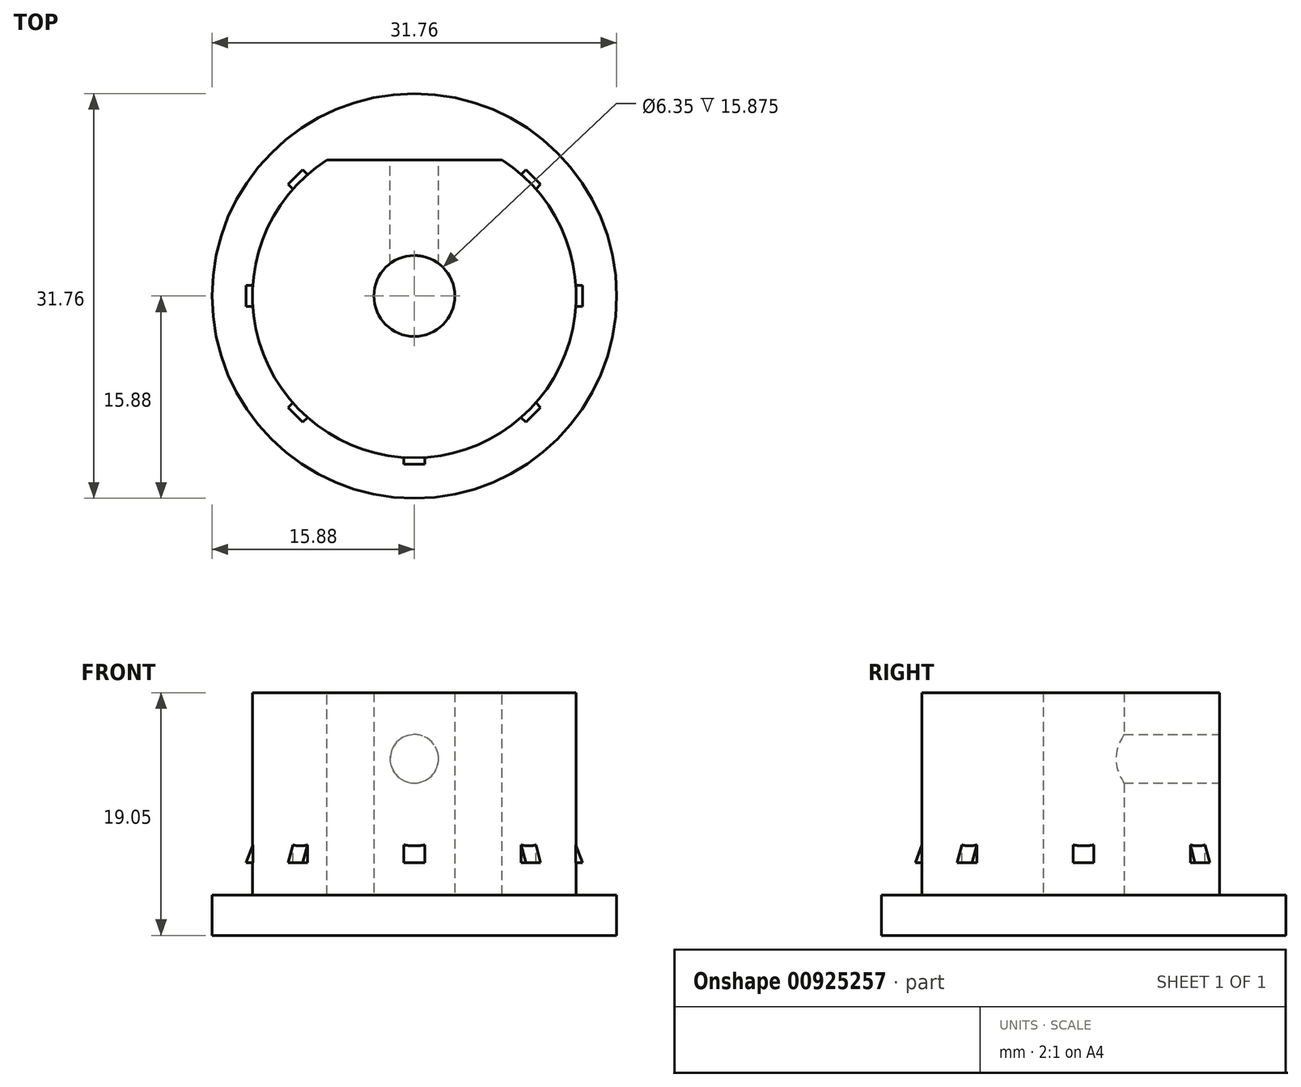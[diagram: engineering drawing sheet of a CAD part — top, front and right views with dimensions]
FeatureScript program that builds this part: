
annotation { "Feature Type Name" : "Feature", "Feature Type Description" : "" }
export const myFeature = defineFeature(function(context is Context, id is Id, definition is map)
    precondition{}
    {
        {
            var Q0;
            Q0=qCreatedBy(makeId("Top.planeOp"),FACE);
            var sketch = newSketch(context, id + "F0", { "sketchPlane" : qUnion([Q0])});
            skCircle(sketch, "E0", {"center": v(0, 0) * mm, "radius": 15.88 * mm});
            skCircle(sketch, "E1", {"center": v(0, 0) * mm, "radius": 12.7 * mm});
            skCircle(sketch, "E2", {"center": v(0, 0) * mm, "radius": 3.18 * mm});
            skSolve(sketch);
        }
        {
            var Q0;
            Q0=makeQuery(id+"F0.imprint","IMPRINT",FACE,{"disambiguationData":[TD([[makeQuery(id+"F0.imprint","IMPRINT",EDGE,{"derivedFrom":sQuery(id+"F0.wireOp",EDGE,"E1")}),1.0]])]});
            extrude(context, id + "F1", {"entities" : qUnion([Q0]), "depth" : 19.05 * mm, "offsetDistance" : 25.4 * mm});
        }
        {
            var Q0;
            Q0=makeQuery(id+"F0.imprint","IMPRINT",FACE,{"disambiguationData":[TD([[makeQuery(id+"F0.imprint","IMPRINT",EDGE,{"derivedFrom":sQuery(id+"F0.wireOp",EDGE,"E0")}),1.0]])]});
            extrude(context, id + "F2", {"entities" : qUnion([Q0]), "operationType" : NewBodyOperationType.ADD, "depth" : 3.17 * mm, "offsetDistance" : 25.4 * mm});
        }
        {
            var Q0;
            Q0=makeQuery(id+"F1.opExtrude","CAP_FACE",FACE,{"disambiguationData":[OSD([sQuery(id+"F0.wireOp",EDGE,"E1")])],"isStart":false});
            var sketch = newSketch(context, id + "F3", { "sketchPlane" : qUnion([Q0])});
            skLineSegment(sketch, "E3", {"start": v(-6.87, 10.68) * mm, "end": v(6.87, 10.68) * mm});
            skSolve(sketch);
        }
        {
            var Q0;
            {var subQ0=sQuery(id+"F3.wireOp",EDGE,"E3");Q0=makeQuery(id+"F3.imprint","IMPRINT",FACE,{"disambiguationData":[TD([[makeQuery(id+"F3.imprint","IMPRINT",EDGE,{"derivedFrom":subQ0}),1.0]])]});}
            extrude(context, id + "F4", {"entities" : qUnion([Q0]), "operationType" : NewBodyOperationType.REMOVE, "oppositeDirection" : true, "depth" : 12.7 * mm, "offsetDistance" : 25.4 * mm});
        }
        {
            var Q0;
            Q0=makeQuery(id+"F0.imprint","IMPRINT",FACE,{"disambiguationData":[TD([[makeQuery(id+"F0.imprint","IMPRINT",EDGE,{"derivedFrom":sQuery(id+"F0.wireOp",EDGE,"E2")}),1.0]])]});
            extrude(context, id + "F5", {"entities" : qUnion([Q0]), "operationType" : NewBodyOperationType.ADD, "depth" : 3.17 * mm, "offsetDistance" : 25.4 * mm});
        }
        {
            var Q0;
            Q0=makeQuery(id+"F4.boolean.opBoolean","COPY",FACE,{"derivedFrom":makeQuery(id+"F4.opExtrude","SWEPT_FACE",FACE,{"disambiguationData":[OSD([sQuery(id+"F3.wireOp",EDGE,"E3")])]})});
            var sketch = newSketch(context, id + "F6", { "sketchPlane" : qUnion([Q0])});
            skCircle(sketch, "E4", {"center": v(0, 13.86) * mm, "radius": 1.9 * mm});
            skSolve(sketch);
        }
        {
            var Q0;
            Q0=makeQuery(id+"F6.imprint","IMPRINT",FACE,{"disambiguationData":[TD([[makeQuery(id+"F6.imprint","IMPRINT",EDGE,{"derivedFrom":sQuery(id+"F6.wireOp",EDGE,"E4")}),1.0]])]});
            extrude(context, id + "F7", {"entities" : qUnion([Q0]), "operationType" : NewBodyOperationType.REMOVE, "oppositeDirection" : true, "depth" : 12.7 * mm, "offsetDistance" : 25.4 * mm});
        }
        {
            var Q0;
            Q0=makeQuery(id+"F1.opExtrude","CAP_FACE",FACE,{"disambiguationData":[OSD([sQuery(id+"F0.wireOp",EDGE,"E1"),sQuery(id+"F0.wireOp",EDGE,"E2")])],"isStart":false});
            var sketch = newSketch(context, id + "F8", { "sketchPlane" : qUnion([Q0])});
            skLineSegment(sketch, "E5", {"start": v(-12.7, 0) * mm, "end": v(12.7, 0) * mm, "construction": true});
            skLineSegment(sketch, "E6", {"start": v(12.7, 0) * mm, "end": v(13.2, 0) * mm, "construction": true});
            skLineSegment(sketch, "E7.left", {"start": v(13.2, 0.82) * mm, "end": v(13.2, -0.82) * mm});
            skPoint(sketch, "E7.middle", {"position": v(12.7, 0) * mm});
            skPoint(sketch, "E8.orphan", {"position": v(12.2, 0.82) * mm});
            skPoint(sketch, "E7.top.end.orphan", {"position": v(12.2, -0.82) * mm});
            skLineSegment(sketch, "E9", {"start": v(13.2, -0.82) * mm, "end": v(12.67, -0.82) * mm});
            skLineSegment(sketch, "E10", {"start": v(13.2, 0.82) * mm, "end": v(12.67, 0.82) * mm});
            skSolve(sketch);
        }
        {
            var Q0;
            Q0=makeQuery(id+"F8.imprint","IMPRINT",FACE,{"disambiguationData":[TD([[makeQuery(id+"F8.imprint","IMPRINT",EDGE,{"derivedFrom":sQuery(id+"F8.wireOp",EDGE,"E7.left")}),-1.0]])]});
            extrude(context, id + "F9", {"entities" : qUnion([Q0]), "oppositeDirection" : true, "depth" : 13.33 * mm, "offsetDistance" : 25.4 * mm});
        }
        {
            var Q0;
            Q0=makeQuery(id+"F9.opExtrude","CAP_EDGE",EDGE,{"disambiguationData":[OSD([sQuery(id+"F8.wireOp",EDGE,"E7.left")])],"isStart":true});
            chamfer(context, id + "F10", {"entities" : qUnion([Q0]), "chamferType" : ChamferType.TWO_OFFSETS, "width1" : 13.33 * mm, "oppositeDirection" : false, "width2" : 5.08 * mm, "tangentPropagation" : true});
        }
        {
            var Q0;
            Q0=qCreatedBy(makeId("Right.planeOp"),FACE);
            var sketch = newSketch(context, id + "F11", { "sketchPlane" : qUnion([Q0])});
            skLineSegment(sketch, "E11", {"start": v(0, 0) * mm, "end": v(0, 25.06) * mm, "construction": true});
            skSolve(sketch);
        }
        {
            var Q0;
            Q0=makeQuery(id+"F9.opExtrude","SWEPT_BODY",BODY,{"disambiguationData":[OSD([sQuery(id+"F0.wireOp",EDGE,"E1"),sQuery(id+"F8.wireOp",EDGE,"E7.left"),sQuery(id+"F8.wireOp",EDGE,"E9"),sQuery(id+"F8.wireOp",EDGE,"E10")])]});
            var Q1;
            Q1=sQuery(id+"F11.wireOp",EDGE,"E11");
            circularPattern(context, id + "F12", {"entities" : qUnion([Q0]), "axis" : qUnion([Q1]), "angle" : 360 * degree, "instanceCount" : 8, "equalSpace" : true, "computeTransformsWithoutBuiltin" : true});
        }
        {
            var Q0;
            Q0=makeQuery(id+"F12.opPattern","COPY",BODY,{"derivedFrom":makeQuery(id+"F9.opExtrude","SWEPT_BODY",BODY,{"disambiguationData":[OSD([sQuery(id+"F0.wireOp",EDGE,"E1"),sQuery(id+"F8.wireOp",EDGE,"E7.left"),sQuery(id+"F8.wireOp",EDGE,"E9"),sQuery(id+"F8.wireOp",EDGE,"E10")])]}),"instanceName":"2"});
            deleteBodies(context, id + "F13", {"entities" : qUnion([Q0])});
        }
        {
            var Q0;
            Q0=makeQuery(id+"F4.boolean.opBoolean","COPY",FACE,{"derivedFrom":makeQuery(id+"F4.opExtrude","CAP_FACE",FACE,{"disambiguationData":[OSD([sQuery(id+"F0.wireOp",EDGE,"E1"),sQuery(id+"F3.wireOp",EDGE,"E3")])],"isStart":false})});
            var Q1;
            Q1=makeQuery(id+"F2.opExtrude","CAP_FACE",FACE,{"disambiguationData":[OSD([sQuery(id+"F0.wireOp",EDGE,"E0"),sQuery(id+"F0.wireOp",EDGE,"E1")])],"isStart":false});
            extrude(context, id + "F14", {"entities" : qUnion([Q0]), "operationType" : NewBodyOperationType.REMOVE, "endBound" : BoundingType.UP_TO_SURFACE, "oppositeDirection" : true, "depth" : 25.4 * mm, "endBoundEntityFace" : qUnion([Q1]), "offsetDistance" : 25.4 * mm});
        }
    });
